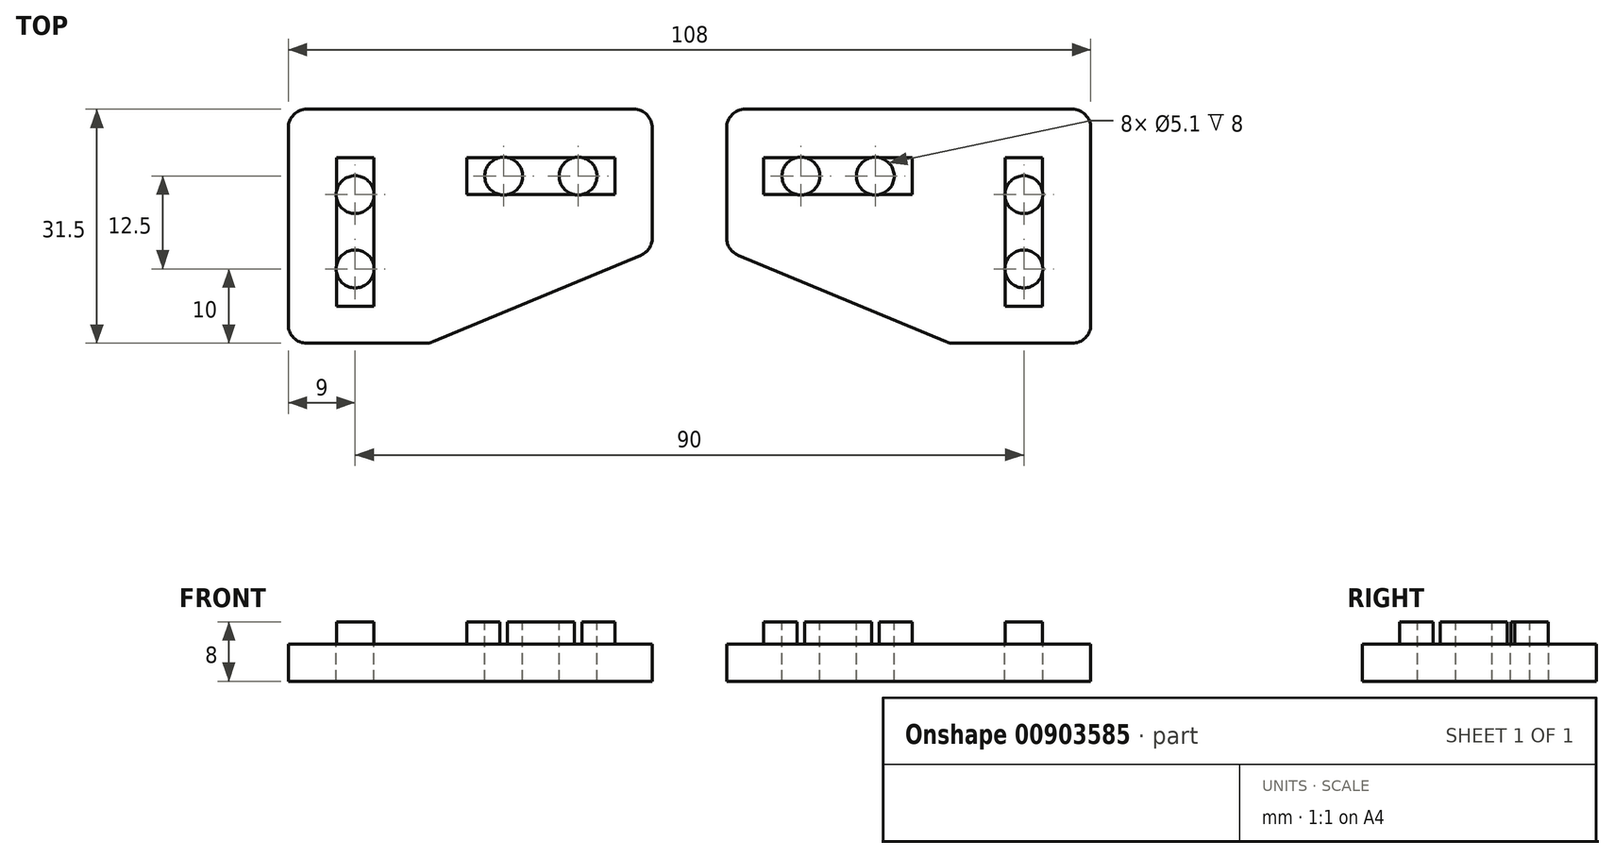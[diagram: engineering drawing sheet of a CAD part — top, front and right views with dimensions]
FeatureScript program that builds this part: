
annotation { "Feature Type Name" : "Feature", "Feature Type Description" : "" }
export const myFeature = defineFeature(function(context is Context, id is Id, definition is map)
    precondition{}
    {
        {
            var Q0;
            Q0=qCreatedBy(makeId("Top.planeOp"),FACE);
            var sketch = newSketch(context, id + "F0", { "sketchPlane" : qUnion([Q0])});
            skLineSegment(sketch, "E0", {"start": v(-9, -1) * mm, "end": v(40, -1) * mm});
            skLineSegment(sketch, "E1", {"start": v(40, -1) * mm, "end": v(40, -20) * mm});
            skLineSegment(sketch, "E2", {"start": v(-9, -1) * mm, "end": v(-9, -32.5) * mm});
            skLineSegment(sketch, "E3", {"start": v(-9, -32.5) * mm, "end": v(10, -32.5) * mm});
            skLineSegment(sketch, "E4.bottom", {"start": v(2.5, -7.5) * mm, "end": v(-2.5, -7.5) * mm, "construction": true});
            skLineSegment(sketch, "E4.top", {"start": v(2.5, -27.5) * mm, "end": v(-2.5, -27.5) * mm, "construction": true});
            skLineSegment(sketch, "E4.left", {"start": v(2.5, -7.5) * mm, "end": v(2.5, -27.5) * mm, "construction": true});
            skLineSegment(sketch, "E4.right", {"start": v(-2.5, -7.5) * mm, "end": v(-2.5, -27.5) * mm, "construction": true});
            skPoint(sketch, "E4.middle", {"position": v(0, -17.5) * mm});
            skLineSegment(sketch, "E5.bottom", {"start": v(15, -7.5) * mm, "end": v(35, -7.5) * mm, "construction": true});
            skLineSegment(sketch, "E5.top", {"start": v(15, -12.5) * mm, "end": v(35, -12.5) * mm, "construction": true});
            skLineSegment(sketch, "E5.left", {"start": v(15, -7.5) * mm, "end": v(15, -12.5) * mm, "construction": true});
            skLineSegment(sketch, "E5.right", {"start": v(35, -7.5) * mm, "end": v(35, -12.5) * mm, "construction": true});
            skPoint(sketch, "E5.middle", {"position": v(25, -10) * mm});
            skLineSegment(sketch, "E6", {"start": v(10, -32.5) * mm, "end": v(40, -20) * mm});
            skSolve(sketch);
        }
        {
            var Q0;
            Q0=makeQuery(id+"F0.imprint","IMPRINT",FACE,{"disambiguationData":[TD([[makeQuery(id+"F0.imprint","IMPRINT",EDGE,{"derivedFrom":sQuery(id+"F0.wireOp",EDGE,"E0")}),-1.0]])]});
            extrude(context, id + "F1", {"entities" : qUnion([Q0]), "oppositeDirection" : true, "depth" : 5 * mm});
        }
        {
            var Q0;
            Q0=qCreatedBy(makeId("Top.planeOp"),FACE);
            var sketch = newSketch(context, id + "F2", { "sketchPlane" : qUnion([Q0])});
            skLineSegment(sketch, "E7.0", {"start": v(2.5, -7.5) * mm, "end": v(-2.5, -7.5) * mm});
            skLineSegment(sketch, "E8.0", {"start": v(-2.5, -7.5) * mm, "end": v(-2.5, -27.5) * mm});
            skLineSegment(sketch, "E9.0", {"start": v(2.5, -7.5) * mm, "end": v(2.5, -27.5) * mm});
            skLineSegment(sketch, "E10.0", {"start": v(2.5, -27.5) * mm, "end": v(-2.5, -27.5) * mm});
            skLineSegment(sketch, "E11.0", {"start": v(15, -7.5) * mm, "end": v(15, -12.5) * mm});
            skLineSegment(sketch, "E12.0", {"start": v(15, -7.5) * mm, "end": v(35, -7.5) * mm});
            skLineSegment(sketch, "E13.0", {"start": v(15, -12.5) * mm, "end": v(35, -12.5) * mm});
            skLineSegment(sketch, "E14.0", {"start": v(35, -7.5) * mm, "end": v(35, -12.5) * mm});
            skSolve(sketch);
        }
        {
            var Q0;
            Q0=qSketchRegion(id+"F2",true);
            extrude(context, id + "F3", {"entities" : qUnion([Q0]), "operationType" : NewBodyOperationType.ADD, "depth" : 3 * mm});
        }
        {
            var Q0;
            Q0=makeQuery(id+"F3.opExtrude","CAP_FACE",FACE,{"disambiguationData":[OSD([sQuery(id+"F2.wireOp",EDGE,"E7.0"),sQuery(id+"F2.wireOp",EDGE,"E8.0"),sQuery(id+"F2.wireOp",EDGE,"E9.0"),sQuery(id+"F2.wireOp",EDGE,"E10.0")])],"isStart":false});
            var sketch = newSketch(context, id + "F4", { "sketchPlane" : qUnion([Q0])});
            skCircle(sketch, "E15", {"center": v(0, -12.5) * mm, "radius": 2.55 * mm});
            skPoint(sketch, "E15.centerSnap0", {"position": v(0, -7.5) * mm});
            skCircle(sketch, "E16", {"center": v(0, -22.5) * mm, "radius": 2.55 * mm});
            skCircle(sketch, "E17", {"center": v(20, -10) * mm, "radius": 2.55 * mm});
            skCircle(sketch, "E18", {"center": v(30, -10) * mm, "radius": 2.55 * mm});
            skLineSegment(sketch, "E19", {"start": v(0, -12.5) * mm, "end": v(0, -22.5) * mm});
            skLineSegment(sketch, "E20", {"start": v(20, -10) * mm, "end": v(30, -10) * mm});
            skSolve(sketch);
        }
        {
            var Q0;
            Q0=qSketchRegion(id+"F4",true);
            extrude(context, id + "F5", {"entities" : qUnion([Q0]), "operationType" : NewBodyOperationType.REMOVE, "oppositeDirection" : true, "depth" : 10 * mm});
        }
        {
            var Q0;
            Q0=makeQuery(id+"F1.opExtrude","SWEPT_EDGE",EDGE,{"disambiguationData":[OSD([sQuery(id+"F0.wireOp",EDGE,"E0"),sQuery(id+"F0.wireOp",EDGE,"E2")])]});
            var Q1;
            Q1=makeQuery(id+"F1.opExtrude","SWEPT_EDGE",EDGE,{"disambiguationData":[OSD([sQuery(id+"F0.wireOp",EDGE,"E2"),sQuery(id+"F0.wireOp",EDGE,"E3")])]});
            var Q2;
            Q2=makeQuery(id+"F1.opExtrude","SWEPT_EDGE",EDGE,{"disambiguationData":[OSD([sQuery(id+"F0.wireOp",EDGE,"E3"),sQuery(id+"F0.wireOp",EDGE,"E6")])]});
            var Q3;
            Q3=makeQuery(id+"F1.opExtrude","SWEPT_EDGE",EDGE,{"disambiguationData":[OSD([sQuery(id+"F0.wireOp",EDGE,"E1"),sQuery(id+"F0.wireOp",EDGE,"E6")])]});
            var Q4;
            Q4=makeQuery(id+"F1.opExtrude","SWEPT_EDGE",EDGE,{"disambiguationData":[OSD([sQuery(id+"F0.wireOp",EDGE,"E0"),sQuery(id+"F0.wireOp",EDGE,"E1")])]});
            fillet(context, id + "F6", {"entities" : qUnion([Q0, Q1, Q2, Q3, Q4]), "radius" : 2.5 * mm, "tangentPropagation" : true, "allowEdgeOverflow" : false});
        }
        {
            var Q0;
            Q0=makeQuery(id+"F1.opExtrude","SWEPT_FACE",FACE,{"disambiguationData":[OSD([sQuery(id+"F0.wireOp",EDGE,"E1")])]});
            cPlane(context, id + "F7", {"entities" : qUnion([Q0]), "cplaneType" : CPlaneType.OFFSET, "offset" : 5 * mm, "width" : 150 * mm, "height" : 150 * mm});
        }
        {
            var Q0;
            Q0=makeQuery(id+"F1.opExtrude","SWEPT_BODY",BODY,{"disambiguationData":[OSD([sQuery(id+"F0.wireOp",EDGE,"E0"),sQuery(id+"F0.wireOp",EDGE,"E1"),sQuery(id+"F0.wireOp",EDGE,"E2"),sQuery(id+"F0.wireOp",EDGE,"E3"),sQuery(id+"F0.wireOp",EDGE,"E6")])]});
            var Q1;
            Q1=qCreatedBy(id+"F7.planeOp",FACE);
            mirror(context, id + "F8", {"entities" : qUnion([Q0]), "mirrorPlane" : qUnion([Q1])});
        }
    });
